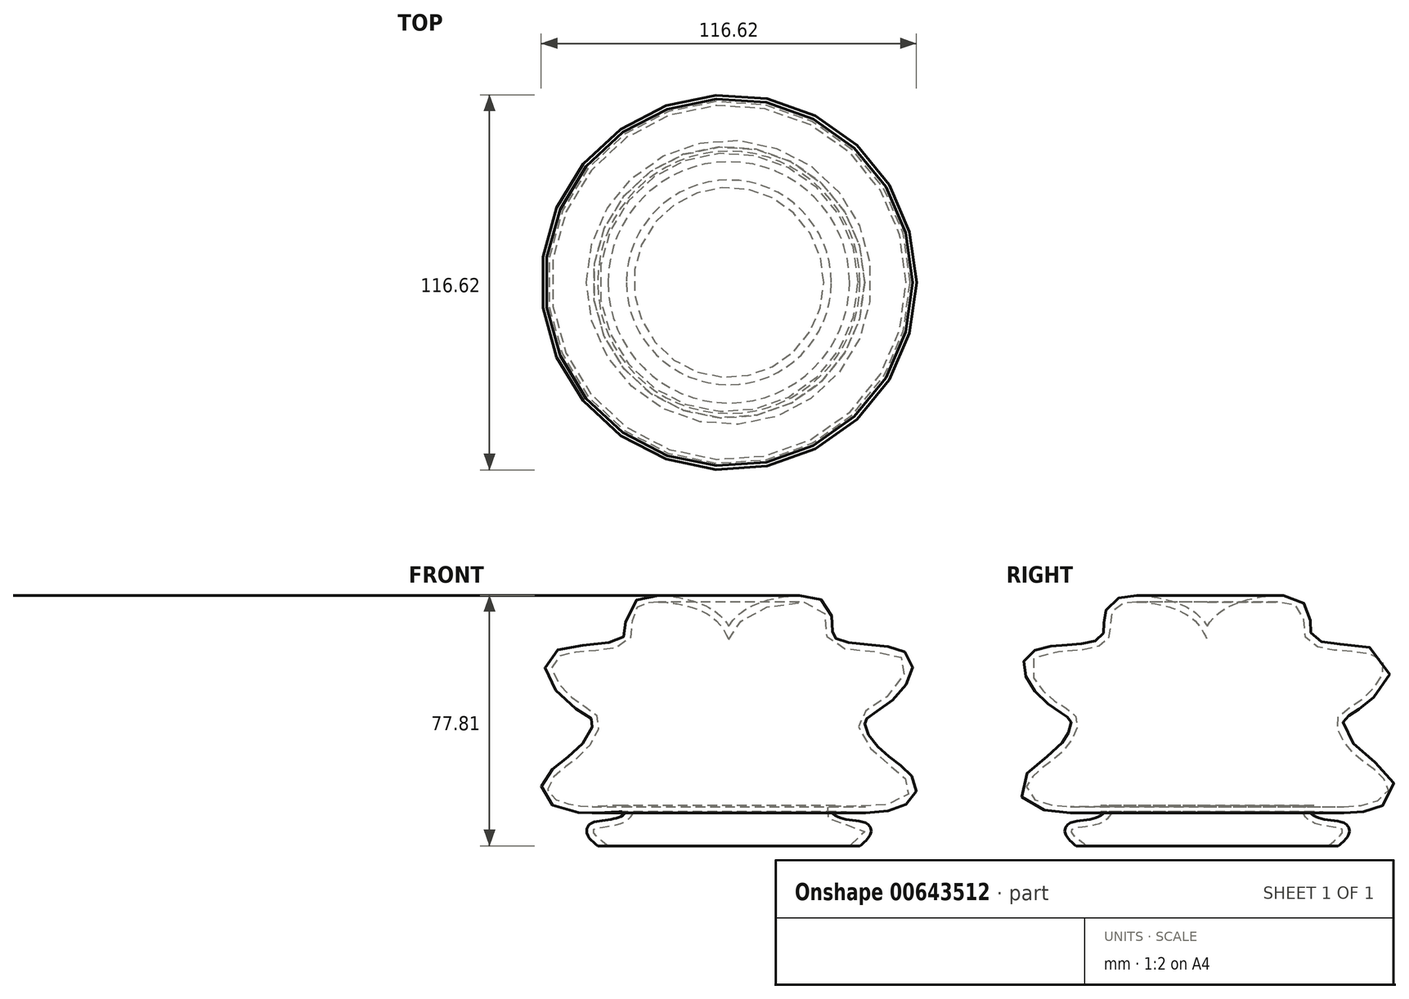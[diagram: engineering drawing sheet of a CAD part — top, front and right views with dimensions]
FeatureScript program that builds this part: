
annotation { "Feature Type Name" : "Feature", "Feature Type Description" : "" }
export const myFeature = defineFeature(function(context is Context, id is Id, definition is map)
    precondition{}
    {
        {
            var Q0;
            Q0=qCreatedBy(makeId("Top.planeOp"),FACE);
            var sketch = newSketch(context, id + "F0", { "sketchPlane" : qUnion([Q0])});
            skCircle(sketch, "E0", {"center": v(0, 0) * mm, "radius": 37.5 * mm});
            skSolve(sketch);
        }
        {
            var Q0;
            Q0=qCreatedBy(makeId("Front.planeOp"),FACE);
            var sketch = newSketch(context, id + "F1", { "sketchPlane" : qUnion([Q0])});
            skLineSegment(sketch, "E1.0", {"start": v(0, 0) * mm, "end": v(37.5, 0) * mm});
            skLineSegment(sketch, "E2", {"start": v(0, 0) * mm, "end": v(0, 64.12) * mm});
            skPoint(sketch, "E3.orphan", {"position": v(-37.5, 0) * mm});
            skFitSpline(sketch, "E4", {"points": [v(0, 64.12) * mm, v(7.57, 72.54) * mm, v(28.81, 73.9) * mm, v(30.84, 64.12) * mm, v(45.53, 60.33) * mm, v(55.02, 56.72) * mm, v(48.24, 45.65) * mm, v(40.34, 39.32) * mm, v(44.63, 29.6) * mm, v(53.44, 22.37) * mm, v(56.15, 16.72) * mm, v(43.95, 12.2) * mm, v(29.71, 11.75) * mm, v(32.88, 7.23) * mm, v(42.14, 4.97) * mm, v(37.5, 0) * mm], "startDerivative": vector(67.62, 135.48) * mm, "endDerivative": vector(-149.57, -114.92) * mm});
            skSolve(sketch);
        }
        {
            var Q0;
            Q0=makeQuery(id+"F1.imprint","IMPRINT",FACE,{"disambiguationData":[TD([[makeQuery(id+"F1.imprint","IMPRINT",EDGE,{"derivedFrom":sQuery(id+"F1.wireOp",EDGE,"E1.0")}),1.0]])]});
            var Q1;
            Q1=sQuery(id+"F1.wireOp",EDGE,"E2");
            revolve(context, id + "F2", {"entities" : qUnion([Q0]), "axis" : qUnion([Q1]), "revolveType" : RevolveType.FULL});
        }
        {
            var Q0;
            Q0=makeQuery(id+"F2.opRevolve","SWEPT_FACE",FACE,{"disambiguationData":[OSD([sQuery(id+"F1.wireOp",EDGE,"E1.0")])]});
            var Q1;
            Q1=makeQuery(id+"F2.opRevolve","SWEPT_BODY",BODY,{"disambiguationData":[OSD([sQuery(id+"F1.wireOp",EDGE,"E1.0"),sQuery(id+"F1.wireOp",EDGE,"E2"),sQuery(id+"F1.wireOp",EDGE,"E4")])]});
            shell(context, id + "F3", {"entities" : qUnion([Q0]), "parts" : qUnion([Q1]), "thickness" : 2 * mm, "oppositeDirection" : true});
        }
    });
